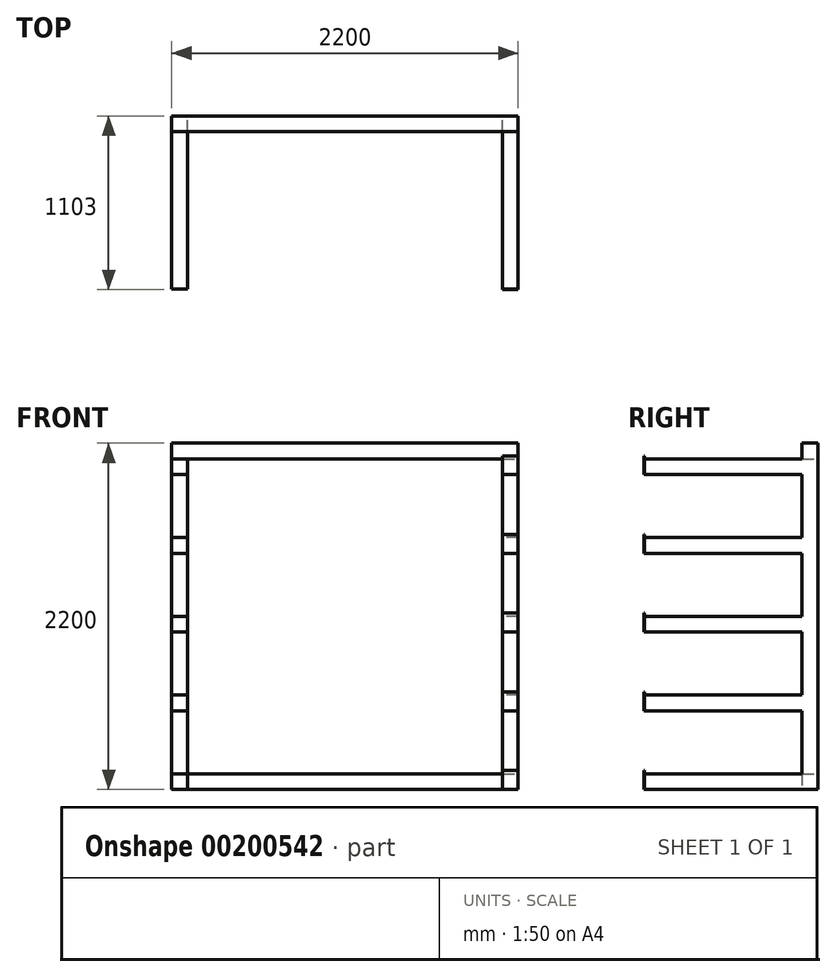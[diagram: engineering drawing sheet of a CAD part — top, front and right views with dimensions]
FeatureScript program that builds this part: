
annotation { "Feature Type Name" : "Feature", "Feature Type Description" : "" }
export const myFeature = defineFeature(function(context is Context, id is Id, definition is map)
    precondition{}
    {
        {
            var Q0;
            Q0=qCreatedBy(makeId("Front.planeOp"),FACE);
            var sketch = newSketch(context, id + "F0", { "sketchPlane" : qUnion([Q0])});
            skLineSegment(sketch, "E0.bottom", {"start": v(0, 0) * mm, "end": v(100, 0) * mm});
            skLineSegment(sketch, "E0.top", {"start": v(0, -2200) * mm, "end": v(100, -2200) * mm});
            skLineSegment(sketch, "E0.left", {"start": v(0, 0) * mm, "end": v(0, -2200) * mm});
            skLineSegment(sketch, "E0.right", {"start": v(100, 0) * mm, "end": v(100, -2200) * mm});
            skLineSegment(sketch, "E1.bottom", {"start": v(100, 0) * mm, "end": v(2100, 0) * mm});
            skLineSegment(sketch, "E1.top", {"start": v(100, -100) * mm, "end": v(2100, -100) * mm});
            skLineSegment(sketch, "E1.left", {"start": v(100, 0) * mm, "end": v(100, -100) * mm});
            skLineSegment(sketch, "E1.right", {"start": v(2100, 0) * mm, "end": v(2100, -100) * mm});
            skLineSegment(sketch, "E2.bottom", {"start": v(100, -2200) * mm, "end": v(2100, -2200) * mm});
            skLineSegment(sketch, "E2.top", {"start": v(100, -2100) * mm, "end": v(2100, -2100) * mm});
            skLineSegment(sketch, "E2.left", {"start": v(100, -2100) * mm, "end": v(100, -2200) * mm});
            skLineSegment(sketch, "E2.right", {"start": v(2100, -2100) * mm, "end": v(2100, -2200) * mm});
            skLineSegment(sketch, "E3.bottom", {"start": v(2100, 0) * mm, "end": v(2200, 0) * mm});
            skLineSegment(sketch, "E3.top", {"start": v(2100, -2200) * mm, "end": v(2200, -2200) * mm});
            skLineSegment(sketch, "E3.left", {"start": v(2100, 0) * mm, "end": v(2100, -2200) * mm});
            skLineSegment(sketch, "E3.right", {"start": v(2200, 0) * mm, "end": v(2200, -2200) * mm});
            skLineSegment(sketch, "E4", {"start": v(1100, 97.76) * mm, "end": v(1100, -2233.4) * mm, "construction": true});
            skPoint(sketch, "E4.startSnap0", {"position": v(1100, 0) * mm});
            skSolve(sketch);
        }
        {
            var Q0;
            Q0=makeQuery(id+"F0.imprint","IMPRINT",FACE,{"disambiguationData":[TD([[makeQuery(id+"F0.imprint","IMPRINT",EDGE,{"derivedFrom":sQuery(id+"F0.wireOp",EDGE,"E0.bottom")}),-1.0]])]});
            var Q1;
            {var subQ0=sQuery(id+"F0.wireOp",EDGE,"E2.bottom");Q1=makeQuery(id+"F0.imprint","IMPRINT",FACE,{"disambiguationData":[TD([[makeQuery(id+"F0.imprint","IMPRINT",EDGE,{"derivedFrom":subQ0}),1.0]])]});}
            var Q2;
            {var subQ3=sQuery(id+"F0.wireOp",EDGE,"E3.bottom");Q2=makeQuery(id+"F0.imprint","IMPRINT",FACE,{"disambiguationData":[TD([[makeQuery(id+"F0.imprint","IMPRINT",EDGE,{"derivedFrom":subQ3}),-1.0]])]});}
            var Q3;
            {var subQ0=sQuery(id+"F0.wireOp",EDGE,"E1.bottom");Q3=makeQuery(id+"F0.imprint","IMPRINT",FACE,{"disambiguationData":[TD([[makeQuery(id+"F0.imprint","IMPRINT",EDGE,{"derivedFrom":subQ0}),-1.0]])]});}
            extrude(context, id + "F1", {"entities" : qUnion([Q0, Q1, Q2, Q3]), "depth" : 100 * mm});
        }
        {
            var Q0;
            Q0=makeQuery(id+"F1.opExtrude","CAP_FACE",FACE,{"disambiguationData":[OSD([sQuery(id+"F0.wireOp",EDGE,"E0.bottom"),sQuery(id+"F0.wireOp",EDGE,"E0.top"),sQuery(id+"F0.wireOp",EDGE,"E0.left"),sQuery(id+"F0.wireOp",EDGE,"E0.right"),sQuery(id+"F0.wireOp",EDGE,"E1.bottom"),sQuery(id+"F0.wireOp",EDGE,"E1.top"),sQuery(id+"F0.wireOp",EDGE,"E2.bottom"),sQuery(id+"F0.wireOp",EDGE,"E2.top"),sQuery(id+"F0.wireOp",EDGE,"E3.bottom"),sQuery(id+"F0.wireOp",EDGE,"E3.top"),sQuery(id+"F0.wireOp",EDGE,"E3.left"),sQuery(id+"F0.wireOp",EDGE,"E3.right")])],"isStart":false});
            var sketch = newSketch(context, id + "F2", { "sketchPlane" : qUnion([Q0])});
            skLineSegment(sketch, "E5", {"start": v(1100, 0) * mm, "end": v(1100, -2200) * mm, "construction": true});
            skLineSegment(sketch, "E6.bottom", {"start": v(100, -100) * mm, "end": v(0, -100) * mm});
            skLineSegment(sketch, "E6.top", {"start": v(100, -200) * mm, "end": v(0, -200) * mm});
            skLineSegment(sketch, "E6.left", {"start": v(100, -100) * mm, "end": v(100, -200) * mm});
            skLineSegment(sketch, "E6.right", {"start": v(0, -100) * mm, "end": v(0, -200) * mm});
            skLineSegment(sketch, "E7.bottom", {"start": v(100, -2100) * mm, "end": v(0, -2100) * mm});
            skLineSegment(sketch, "E7.top", {"start": v(100, -2200) * mm, "end": v(0, -2200) * mm});
            skLineSegment(sketch, "E7.left", {"start": v(100, -2100) * mm, "end": v(100, -2200) * mm});
            skLineSegment(sketch, "E7.right", {"start": v(0, -2100) * mm, "end": v(0, -2200) * mm});
            skLineSegment(sketch, "E8.bottom", {"start": v(0, -1100) * mm, "end": v(100, -1100) * mm});
            skLineSegment(sketch, "E8.top", {"start": v(0, -1200) * mm, "end": v(100, -1200) * mm});
            skLineSegment(sketch, "E8.left", {"start": v(0, -1100) * mm, "end": v(0, -1200) * mm});
            skLineSegment(sketch, "E8.right", {"start": v(100, -1100) * mm, "end": v(100, -1200) * mm});
            skLineSegment(sketch, "E9.bottom", {"start": v(0, -600) * mm, "end": v(100, -600) * mm});
            skLineSegment(sketch, "E9.top", {"start": v(0, -700) * mm, "end": v(100, -700) * mm});
            skLineSegment(sketch, "E9.left", {"start": v(0, -600) * mm, "end": v(0, -700) * mm});
            skLineSegment(sketch, "E9.right", {"start": v(100, -600) * mm, "end": v(100, -700) * mm});
            skLineSegment(sketch, "E10.bottom", {"start": v(0, -1600) * mm, "end": v(100, -1600) * mm});
            skLineSegment(sketch, "E10.top", {"start": v(0, -1700) * mm, "end": v(100, -1700) * mm});
            skLineSegment(sketch, "E10.left", {"start": v(0, -1600) * mm, "end": v(0, -1700) * mm});
            skLineSegment(sketch, "E10.right", {"start": v(100, -1600) * mm, "end": v(100, -1700) * mm});
            skLineSegment(sketch, "E11.MirrorCS", {"start": v(2100, -200) * mm, "end": v(2200, -200) * mm});
            skLineSegment(sketch, "E12.MirrorCS", {"start": v(2100, -100) * mm, "end": v(2100, -200) * mm});
            skLineSegment(sketch, "E13.MirrorCS", {"start": v(2100, -100) * mm, "end": v(2200, -100) * mm});
            skLineSegment(sketch, "E14.MirrorCS", {"start": v(2200, -100) * mm, "end": v(2200, -200) * mm});
            skLineSegment(sketch, "E15.MirrorCS", {"start": v(2200, -600) * mm, "end": v(2100, -600) * mm});
            skLineSegment(sketch, "E16.MirrorCS", {"start": v(2100, -600) * mm, "end": v(2100, -700) * mm});
            skLineSegment(sketch, "E17.MirrorCS", {"start": v(2200, -700) * mm, "end": v(2100, -700) * mm});
            skLineSegment(sketch, "E18.MirrorCS", {"start": v(2200, -600) * mm, "end": v(2200, -700) * mm});
            skLineSegment(sketch, "E19.MirrorCS", {"start": v(2200, -1100) * mm, "end": v(2100, -1100) * mm});
            skLineSegment(sketch, "E20.MirrorCS", {"start": v(2100, -1100) * mm, "end": v(2100, -1200) * mm});
            skLineSegment(sketch, "E21.MirrorCS", {"start": v(2200, -1100) * mm, "end": v(2200, -1200) * mm});
            skLineSegment(sketch, "E22.MirrorCS", {"start": v(2200, -1200) * mm, "end": v(2100, -1200) * mm});
            skLineSegment(sketch, "E23.MirrorCS", {"start": v(2200, -1600) * mm, "end": v(2100, -1600) * mm});
            skLineSegment(sketch, "E24.MirrorCS", {"start": v(2100, -1600) * mm, "end": v(2100, -1700) * mm});
            skLineSegment(sketch, "E25.MirrorCS", {"start": v(2200, -1700) * mm, "end": v(2100, -1700) * mm});
            skLineSegment(sketch, "E26.MirrorCS", {"start": v(2200, -1600) * mm, "end": v(2200, -1700) * mm});
            skLineSegment(sketch, "E27.MirrorCS", {"start": v(2100, -2100) * mm, "end": v(2200, -2100) * mm});
            skLineSegment(sketch, "E28.MirrorCS", {"start": v(2100, -2100) * mm, "end": v(2100, -2200) * mm});
            skLineSegment(sketch, "E29.MirrorCS", {"start": v(2200, -2100) * mm, "end": v(2200, -2200) * mm});
            skLineSegment(sketch, "E30.MirrorCS", {"start": v(2100, -2200) * mm, "end": v(2200, -2200) * mm});
            skSolve(sketch);
        }
        {
            var Q0;
            Q0=makeQuery(id+"F2.imprint","IMPRINT",FACE,{"disambiguationData":[TD([[makeQuery(id+"F2.imprint","IMPRINT",EDGE,{"derivedFrom":sQuery(id+"F2.wireOp",EDGE,"E6.bottom")}),1.0]])]});
            var Q1;
            Q1=makeQuery(id+"F2.imprint","IMPRINT",FACE,{"disambiguationData":[TD([[makeQuery(id+"F2.imprint","IMPRINT",EDGE,{"derivedFrom":sQuery(id+"F2.wireOp",EDGE,"E9.bottom")}),-1.0]])]});
            var Q2;
            Q2=makeQuery(id+"F2.imprint","IMPRINT",FACE,{"disambiguationData":[TD([[makeQuery(id+"F2.imprint","IMPRINT",EDGE,{"derivedFrom":sQuery(id+"F2.wireOp",EDGE,"E8.bottom")}),-1.0]])]});
            var Q3;
            Q3=makeQuery(id+"F2.imprint","IMPRINT",FACE,{"disambiguationData":[TD([[makeQuery(id+"F2.imprint","IMPRINT",EDGE,{"derivedFrom":sQuery(id+"F2.wireOp",EDGE,"E10.bottom")}),-1.0]])]});
            var Q4;
            Q4=makeQuery(id+"F2.imprint","IMPRINT",FACE,{"disambiguationData":[TD([[makeQuery(id+"F2.imprint","IMPRINT",EDGE,{"derivedFrom":sQuery(id+"F2.wireOp",EDGE,"E7.bottom")}),1.0]])]});
            var Q5;
            Q5=makeQuery(id+"F2.imprint","IMPRINT",FACE,{"disambiguationData":[TD([[makeQuery(id+"F2.imprint","IMPRINT",EDGE,{"derivedFrom":sQuery(id+"F2.wireOp",EDGE,"E27.MirrorCS")}),-1.0]])]});
            var Q6;
            Q6=makeQuery(id+"F2.imprint","IMPRINT",FACE,{"disambiguationData":[TD([[makeQuery(id+"F2.imprint","IMPRINT",EDGE,{"derivedFrom":sQuery(id+"F2.wireOp",EDGE,"E23.MirrorCS")}),1.0]])]});
            var Q7;
            Q7=makeQuery(id+"F2.imprint","IMPRINT",FACE,{"disambiguationData":[TD([[makeQuery(id+"F2.imprint","IMPRINT",EDGE,{"derivedFrom":sQuery(id+"F2.wireOp",EDGE,"E19.MirrorCS")}),1.0]])]});
            var Q8;
            Q8=makeQuery(id+"F2.imprint","IMPRINT",FACE,{"disambiguationData":[TD([[makeQuery(id+"F2.imprint","IMPRINT",EDGE,{"derivedFrom":sQuery(id+"F2.wireOp",EDGE,"E17.MirrorCS")}),-1.0]])]});
            var Q9;
            Q9=makeQuery(id+"F2.imprint","IMPRINT",FACE,{"disambiguationData":[TD([[makeQuery(id+"F2.imprint","IMPRINT",EDGE,{"derivedFrom":sQuery(id+"F2.wireOp",EDGE,"E11.MirrorCS")}),1.0]])]});
            extrude(context, id + "F3", {"entities" : qUnion([Q0, Q1, Q2, Q3, Q4, Q5, Q6, Q7, Q8, Q9]), "operationType" : NewBodyOperationType.ADD, "depth" : 1000 * mm});
        }
        {
            var Q0;
            Q0=makeQuery(id+"F3.boolean.opBoolean","MERGE",FACE,{"derivedFrom":[makeQuery(id+"F1.opExtrude","SWEPT_FACE",FACE,{"disambiguationData":[OSD([sQuery(id+"F0.wireOp",EDGE,"E3.right")])]}),makeQuery(id+"F3.opExtrude","SWEPT_FACE",FACE,{"disambiguationData":[OSD([sQuery(id+"F2.wireOp",EDGE,"E14.MirrorCS")])]}),makeQuery(id+"F3.opExtrude","SWEPT_FACE",FACE,{"disambiguationData":[OSD([sQuery(id+"F2.wireOp",EDGE,"E18.MirrorCS")])]}),makeQuery(id+"F3.opExtrude","SWEPT_FACE",FACE,{"disambiguationData":[OSD([sQuery(id+"F2.wireOp",EDGE,"E21.MirrorCS")])]}),makeQuery(id+"F3.opExtrude","SWEPT_FACE",FACE,{"disambiguationData":[OSD([sQuery(id+"F2.wireOp",EDGE,"E26.MirrorCS")])]}),makeQuery(id+"F3.opExtrude","SWEPT_FACE",FACE,{"disambiguationData":[OSD([sQuery(id+"F2.wireOp",EDGE,"E29.MirrorCS")])]})]});
            var sketch = newSketch(context, id + "F4", { "sketchPlane" : qUnion([Q0])});
            skLineSegment(sketch, "E31.bottom", {"start": v(-1100, -200) * mm, "end": v(-1103, -200) * mm});
            skLineSegment(sketch, "E31.top", {"start": v(-1100, -80) * mm, "end": v(-1103, -80) * mm});
            skLineSegment(sketch, "E31.left", {"start": v(-1100, -200) * mm, "end": v(-1100, -80) * mm});
            skLineSegment(sketch, "E31.right", {"start": v(-1103, -200) * mm, "end": v(-1103, -80) * mm});
            skLineSegment(sketch, "E32.bottom", {"start": v(-1100, -700) * mm, "end": v(-1103, -700) * mm});
            skLineSegment(sketch, "E32.top", {"start": v(-1100, -580) * mm, "end": v(-1103, -580) * mm});
            skLineSegment(sketch, "E32.left", {"start": v(-1100, -700) * mm, "end": v(-1100, -580) * mm});
            skLineSegment(sketch, "E32.right", {"start": v(-1103, -700) * mm, "end": v(-1103, -580) * mm});
            skLineSegment(sketch, "E33.bottom", {"start": v(-1100, -1200) * mm, "end": v(-1103, -1200) * mm});
            skLineSegment(sketch, "E33.top", {"start": v(-1100, -1080) * mm, "end": v(-1103, -1080) * mm});
            skLineSegment(sketch, "E33.left", {"start": v(-1100, -1200) * mm, "end": v(-1100, -1080) * mm});
            skLineSegment(sketch, "E33.right", {"start": v(-1103, -1200) * mm, "end": v(-1103, -1080) * mm});
            skLineSegment(sketch, "E34.bottom", {"start": v(-1100, -1700) * mm, "end": v(-1103, -1700) * mm});
            skLineSegment(sketch, "E34.top", {"start": v(-1100, -1580) * mm, "end": v(-1103, -1580) * mm});
            skLineSegment(sketch, "E34.left", {"start": v(-1100, -1700) * mm, "end": v(-1100, -1580) * mm});
            skLineSegment(sketch, "E34.right", {"start": v(-1103, -1700) * mm, "end": v(-1103, -1580) * mm});
            skLineSegment(sketch, "E35.bottom", {"start": v(-1100, -2200) * mm, "end": v(-1103, -2200) * mm});
            skLineSegment(sketch, "E35.top", {"start": v(-1100, -2080) * mm, "end": v(-1103, -2080) * mm});
            skLineSegment(sketch, "E35.left", {"start": v(-1100, -2200) * mm, "end": v(-1100, -2080) * mm});
            skLineSegment(sketch, "E35.right", {"start": v(-1103, -2200) * mm, "end": v(-1103, -2080) * mm});
            skSolve(sketch);
        }
        {
            var Q0;
            {var subQ2=sQuery(id+"F4.wireOp",EDGE,"E35.bottom");Q0=makeQuery(id+"F4.imprint","IMPRINT",FACE,{"disambiguationData":[TD([[makeQuery(id+"F4.imprint","IMPRINT",EDGE,{"derivedFrom":subQ2}),-1.0]])]});}
            var Q1;
            {var subQ5=sQuery(id+"F4.wireOp",EDGE,"E34.bottom");Q1=makeQuery(id+"F4.imprint","IMPRINT",FACE,{"disambiguationData":[TD([[makeQuery(id+"F4.imprint","IMPRINT",EDGE,{"derivedFrom":subQ5}),-1.0]])]});}
            var Q2;
            {var subQ5=sQuery(id+"F4.wireOp",EDGE,"E33.bottom");Q2=makeQuery(id+"F4.imprint","IMPRINT",FACE,{"disambiguationData":[TD([[makeQuery(id+"F4.imprint","IMPRINT",EDGE,{"derivedFrom":subQ5}),-1.0]])]});}
            var Q3;
            {var subQ5=sQuery(id+"F4.wireOp",EDGE,"E32.bottom");Q3=makeQuery(id+"F4.imprint","IMPRINT",FACE,{"disambiguationData":[TD([[makeQuery(id+"F4.imprint","IMPRINT",EDGE,{"derivedFrom":subQ5}),-1.0]])]});}
            var Q4;
            {var subQ5=sQuery(id+"F4.wireOp",EDGE,"E31.bottom");Q4=makeQuery(id+"F4.imprint","IMPRINT",FACE,{"disambiguationData":[TD([[makeQuery(id+"F4.imprint","IMPRINT",EDGE,{"derivedFrom":subQ5}),-1.0]])]});}
            extrude(context, id + "F5", {"entities" : qUnion([Q0, Q1, Q2, Q3, Q4]), "oppositeDirection" : true, "depth" : 100 * mm});
        }
        {
            var Q0;
            Q0=makeQuery(id+"F3.boolean.opBoolean","MERGE",FACE,{"derivedFrom":[makeQuery(id+"F1.opExtrude","SWEPT_FACE",FACE,{"disambiguationData":[OSD([sQuery(id+"F0.wireOp",EDGE,"E0.left")])]}),makeQuery(id+"F3.opExtrude","SWEPT_FACE",FACE,{"disambiguationData":[OSD([sQuery(id+"F2.wireOp",EDGE,"E6.right")])]}),makeQuery(id+"F3.opExtrude","SWEPT_FACE",FACE,{"disambiguationData":[OSD([sQuery(id+"F2.wireOp",EDGE,"E7.right")])]}),makeQuery(id+"F3.opExtrude","SWEPT_FACE",FACE,{"disambiguationData":[OSD([sQuery(id+"F2.wireOp",EDGE,"E8.left")])]}),makeQuery(id+"F3.opExtrude","SWEPT_FACE",FACE,{"disambiguationData":[OSD([sQuery(id+"F2.wireOp",EDGE,"E9.left")])]}),makeQuery(id+"F3.opExtrude","SWEPT_FACE",FACE,{"disambiguationData":[OSD([sQuery(id+"F2.wireOp",EDGE,"E10.left")])]})]});
            var sketch = newSketch(context, id + "F6", { "sketchPlane" : qUnion([Q0])});
            skLineSegment(sketch, "E36.bottom", {"start": v(1100, -200) * mm, "end": v(1100, -200) * mm});
            skLineSegment(sketch, "E36.top", {"start": v(1100, -75.76) * mm, "end": v(1100, -75.76) * mm});
            skLineSegment(sketch, "E36.left", {"start": v(1100, -200) * mm, "end": v(1100, -75.76) * mm});
            skLineSegment(sketch, "E36.right", {"start": v(1100, -200) * mm, "end": v(1100, -75.76) * mm});
            skLineSegment(sketch, "E37.bottom", {"start": v(1100, -200) * mm, "end": v(1103, -200) * mm});
            skLineSegment(sketch, "E37.top", {"start": v(1100, -80) * mm, "end": v(1103, -80) * mm});
            skLineSegment(sketch, "E37.left", {"start": v(1100, -200) * mm, "end": v(1100, -80) * mm});
            skLineSegment(sketch, "E37.right", {"start": v(1103, -200) * mm, "end": v(1103, -80) * mm});
            skLineSegment(sketch, "E38.bottom", {"start": v(1100, -700) * mm, "end": v(1103, -700) * mm});
            skLineSegment(sketch, "E38.top", {"start": v(1100, -580) * mm, "end": v(1103, -580) * mm});
            skLineSegment(sketch, "E38.left", {"start": v(1100, -700) * mm, "end": v(1100, -580) * mm});
            skLineSegment(sketch, "E38.right", {"start": v(1103, -700) * mm, "end": v(1103, -580) * mm});
            skLineSegment(sketch, "E39.bottom", {"start": v(1100, -1200) * mm, "end": v(1103, -1200) * mm});
            skLineSegment(sketch, "E39.top", {"start": v(1100, -1080) * mm, "end": v(1103, -1080) * mm});
            skLineSegment(sketch, "E39.left", {"start": v(1100, -1200) * mm, "end": v(1100, -1080) * mm});
            skLineSegment(sketch, "E39.right", {"start": v(1103, -1200) * mm, "end": v(1103, -1080) * mm});
            skLineSegment(sketch, "E40.bottom", {"start": v(1100, -1700) * mm, "end": v(1103, -1700) * mm});
            skLineSegment(sketch, "E40.top", {"start": v(1100, -1580) * mm, "end": v(1103, -1580) * mm});
            skLineSegment(sketch, "E40.left", {"start": v(1100, -1700) * mm, "end": v(1100, -1580) * mm});
            skLineSegment(sketch, "E40.right", {"start": v(1103, -1700) * mm, "end": v(1103, -1580) * mm});
            skLineSegment(sketch, "E41.bottom", {"start": v(1100, -2200) * mm, "end": v(1103, -2200) * mm});
            skLineSegment(sketch, "E41.top", {"start": v(1100, -2080) * mm, "end": v(1103, -2080) * mm});
            skLineSegment(sketch, "E41.left", {"start": v(1100, -2200) * mm, "end": v(1100, -2080) * mm});
            skLineSegment(sketch, "E41.right", {"start": v(1103, -2200) * mm, "end": v(1103, -2080) * mm});
            skSolve(sketch);
        }
        {
            var Q0;
            Q0=sQuery(id+"F6.wireOp",EDGE,"E41.left");
            var Q1;
            Q1=sQuery(id+"F6.wireOp",EDGE,"E40.right");
            var Q2;
            Q2=sQuery(id+"F6.wireOp",EDGE,"E39.right");
            var Q3;
            Q3=sQuery(id+"F6.wireOp",EDGE,"E38.right");
            var Q4;
            Q4=sQuery(id+"F6.wireOp",EDGE,"E37.left");
            extrude(context, id + "F7", {"bodyType" : ToolBodyType.SURFACE, "surfaceEntities" : qUnion([Q0, Q1, Q2, Q3, Q4]), "oppositeDirection" : true, "depth" : 100 * mm});
        }
    });
